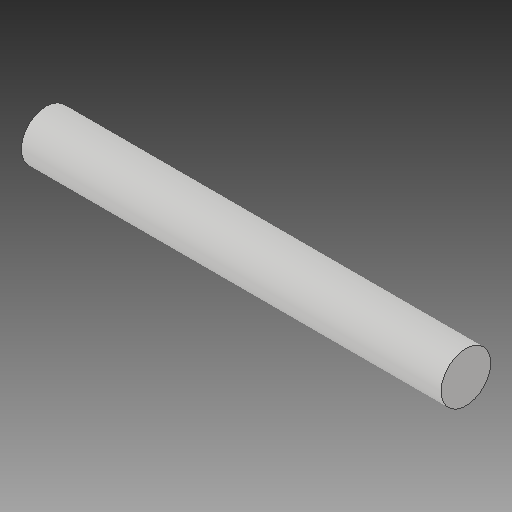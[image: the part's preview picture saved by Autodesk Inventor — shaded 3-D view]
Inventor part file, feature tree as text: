
AUTODESK INVENTOR PART (.ipt)
format: ipt  version: 2017 (Build 210142000, 142)  size: 89,088 bytes
history: native  units: in
note: dims shown in document units (in); Inventor stores cm internally (conversion verified against a paired STEP export)
features: extrude x1, sketch x1
ambient origin geometry x8: Origin, YZ Plane, XZ Plane, XY Plane, X Axis, Y Axis, Z Axis, Center Point
bodies: Solid1 (feature_tree)
feature tree (2):
  extrude  "Extrusion1"  Depth=2.11in TaperAngle=0.0deg
  sketch  "Sketch1"  dims[d0=0.25in d1=2.11in d2=0.0in]
